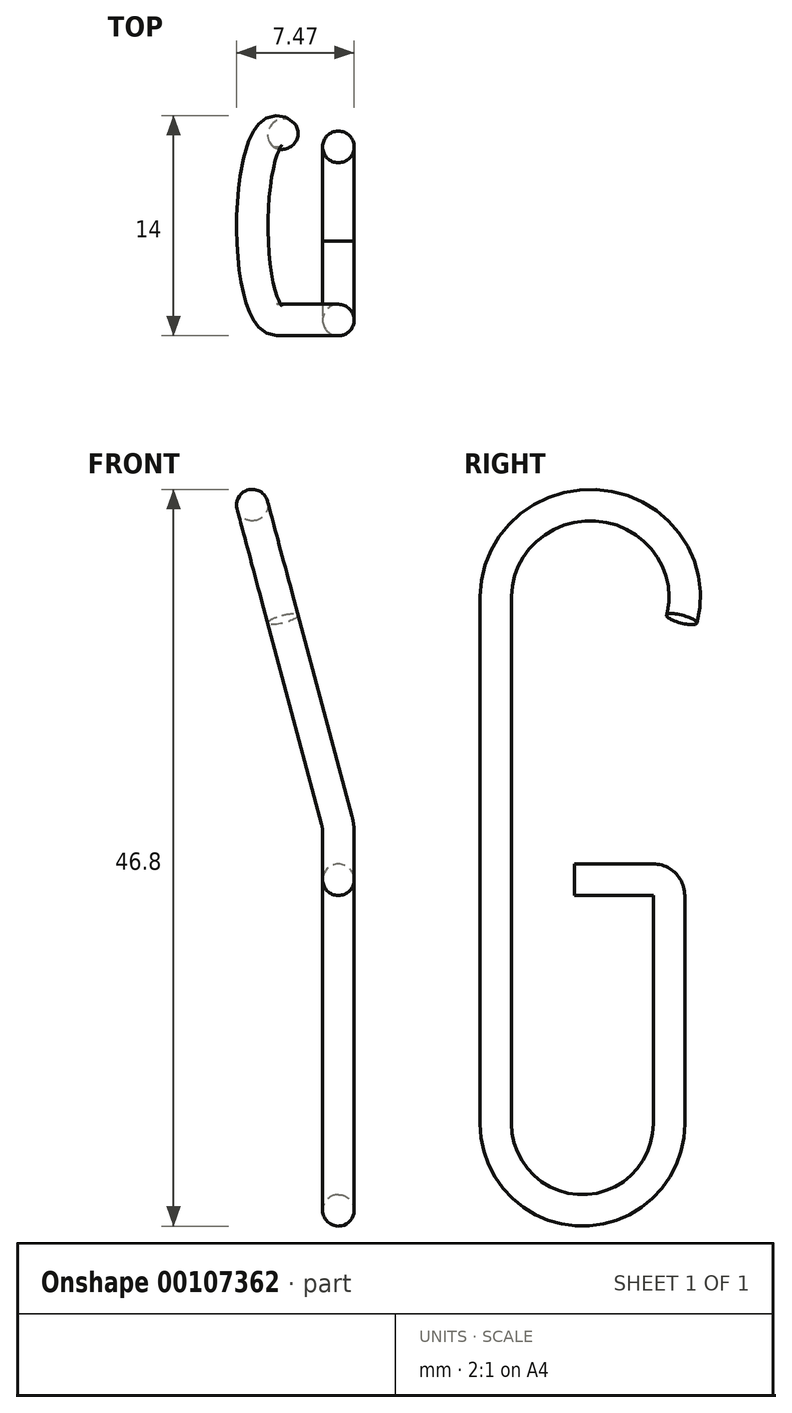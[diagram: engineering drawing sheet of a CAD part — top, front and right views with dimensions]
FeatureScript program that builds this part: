
annotation { "Feature Type Name" : "Feature", "Feature Type Description" : "" }
export const myFeature = defineFeature(function(context is Context, id is Id, definition is map)
    precondition{}
    {
        {
            var Q0;
            Q0=qCreatedBy(makeId("Right.planeOp"),FACE);
            var sketch = newSketch(context, id + "F0", { "sketchPlane" : qUnion([Q0])});
            skLineSegment(sketch, "E0", {"start": v(0, 0) * mm, "end": v(5, 0) * mm});
            skLineSegment(sketch, "E1", {"start": v(6, -1) * mm, "end": v(6, -15.5) * mm});
            skArc(sketch, "E2", {"start": v(-5, -15.5) * mm, "mid": v(0.5, -21) * mm, "end": v(6, -15.5) * mm});
            skLineSegment(sketch, "E3", {"start": v(-5, -15.5) * mm, "end": v(-5, 3) * mm});
            skPoint(sketch, "E4.visualSharp", {"position": v(6, 0) * mm});
            skArc(sketch, "E4.filletArc", {"start": v(6, -1) * mm, "mid": v(5.7, -0.3) * mm, "end": v(5, 0) * mm});
            skSolve(sketch);
        }
        {
            var Q0;
            Q0=qCreatedBy(makeId("Front.planeOp"),FACE);
            var sketch = newSketch(context, id + "F1", { "sketchPlane" : qUnion([Q0])});
            skCircle(sketch, "E5", {"center": v(0, 0) * mm, "radius": 1 * mm});
            skSolve(sketch);
        }
        {
            var Q0;
            Q0=qCreatedBy(makeId("Front.planeOp"),FACE);
            cPlane(context, id + "F2", {"entities" : qUnion([Q0]), "cplaneType" : CPlaneType.OFFSET, "offset" : 5 * mm, "width" : 150 * mm, "height" : 150 * mm});
        }
        {
            var Q0;
            Q0=qCreatedBy(id+"F2.planeOp",FACE);
            var sketch = newSketch(context, id + "F3", { "sketchPlane" : qUnion([Q0])});
            skLineSegment(sketch, "E6", {"start": v(-0.1, 3.78) * mm, "end": v(-3.91, 18) * mm});
            skArc(sketch, "E7", {"start": v(0, 3) * mm, "mid": v(-0.03, 3.4) * mm, "end": v(-0.1, 3.78) * mm});
            skSolve(sketch);
        }
        {
            var Q0;
            Q0=sQuery(id+"F3.wireOp",EDGE,"E6");
            cPlane(context, id + "F4", {"entities" : qUnion([Q0]), "cplaneType" : CPlaneType.LINE_ANGLE, "offset" : 25 * mm, "angle" : 0 * degree, "width" : 150 * mm, "height" : 150 * mm});
        }
        {
            var Q0;
            Q0=qCreatedBy(id+"F4.planeOp",FACE);
            var sketch = newSketch(context, id + "F5", { "sketchPlane" : qUnion([Q0])});
            skArc(sketch, "E8", {"start": v(6.8, 16.9) * mm, "mid": v(1.76, 24.35) * mm, "end": v(-5, 18.4) * mm});
            skSolve(sketch);
        }
        {
            var Q0;
            Q0=makeQuery(id+"F1.imprint","IMPRINT",FACE,{"disambiguationData":[TD([[makeQuery(id+"F1.imprint","IMPRINT",EDGE,{"derivedFrom":sQuery(id+"F1.wireOp",EDGE,"E5")}),1.0]])]});
            var Q1;
            Q1=sQuery(id+"F0.wireOp",EDGE,"E0");
            var Q2;
            Q2=sQuery(id+"F0.wireOp",EDGE,"E4.filletArc");
            var Q3;
            Q3=sQuery(id+"F0.wireOp",EDGE,"E1");
            var Q4;
            Q4=sQuery(id+"F0.wireOp",EDGE,"E2");
            var Q5;
            Q5=sQuery(id+"F0.wireOp",EDGE,"E3");
            var Q6;
            Q6=sQuery(id+"F3.wireOp",EDGE,"E7");
            var Q7;
            Q7=sQuery(id+"F3.wireOp",EDGE,"E6");
            var Q8;
            Q8=sQuery(id+"F5.wireOp",EDGE,"E8");
            sweep(context, id + "F6", {"profiles" : qUnion([Q0]), "path" : qUnion([Q1, Q2, Q3, Q4, Q5, Q6, Q7, Q8])});
        }
    });
